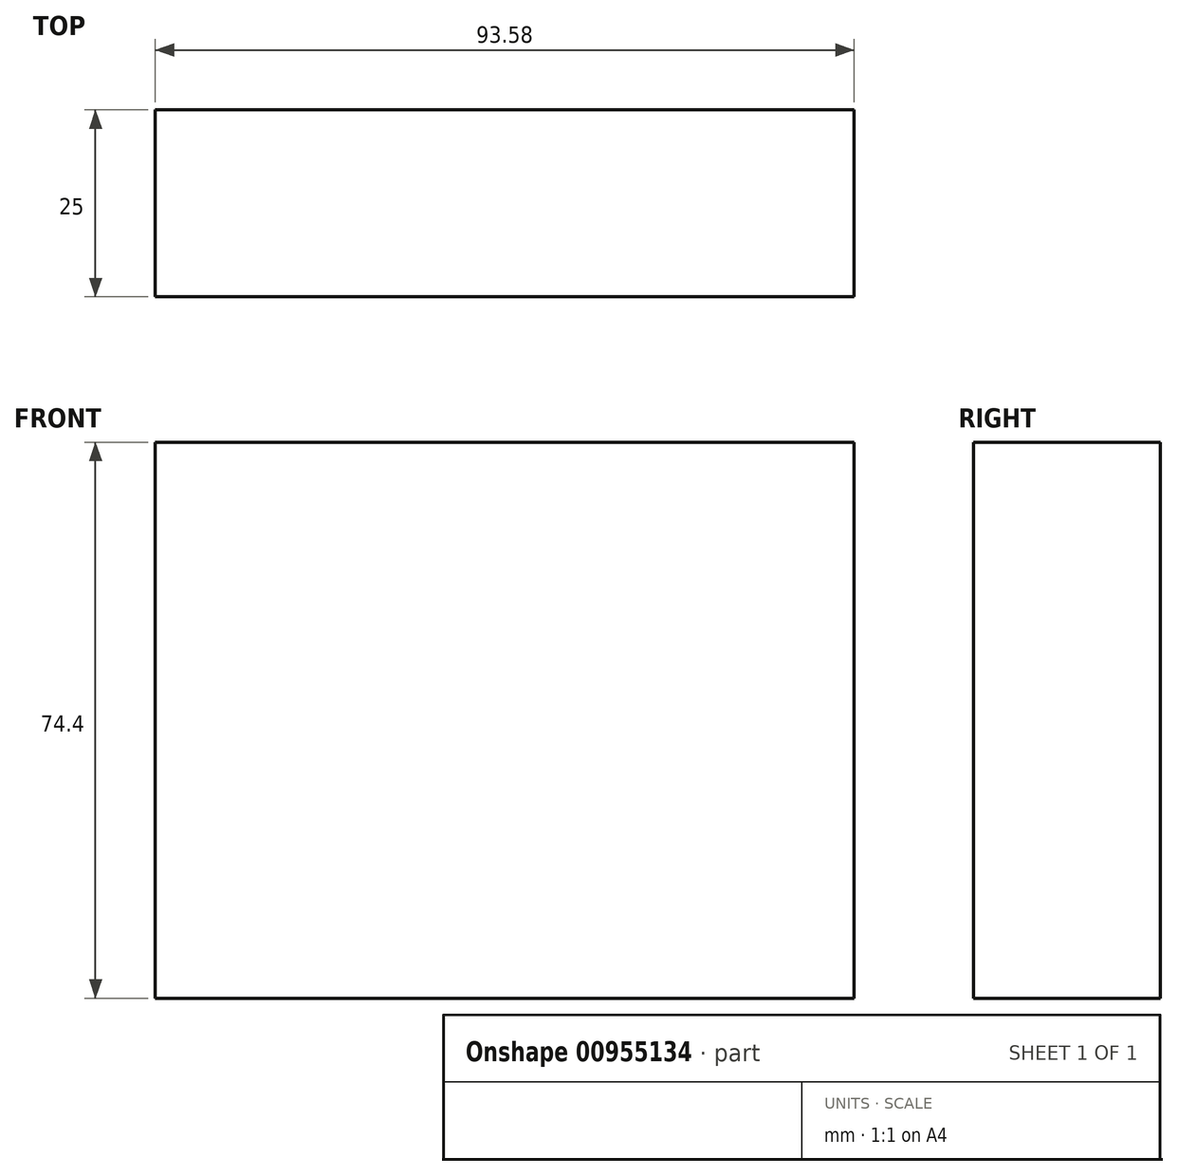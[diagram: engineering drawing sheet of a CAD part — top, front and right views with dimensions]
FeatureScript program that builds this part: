
annotation { "Feature Type Name" : "Feature", "Feature Type Description" : "" }
export const myFeature = defineFeature(function(context is Context, id is Id, definition is map)
    precondition{}
    {
        {
            var Q0;
            Q0=qCreatedBy(makeId("Front.planeOp"),FACE);
            var sketch = newSketch(context, id + "F0", { "sketchPlane" : qUnion([Q0])});
            skLineSegment(sketch, "E0.bottom", {"start": v(-99.12, 58.07) * mm, "end": v(-5.54, 58.07) * mm});
            skLineSegment(sketch, "E0.top", {"start": v(-99.12, -16.33) * mm, "end": v(-5.54, -16.33) * mm});
            skLineSegment(sketch, "E0.left", {"start": v(-99.12, 58.07) * mm, "end": v(-99.12, -16.33) * mm});
            skLineSegment(sketch, "E0.right", {"start": v(-5.54, 58.07) * mm, "end": v(-5.54, -16.33) * mm});
            skSolve(sketch);
        }
        {
            var Q0;
            Q0 = qSketchRegion(id + "F0", true);
            extrude(context, id + "F1", {"entities" : qUnion([Q0]), "depth" : 25 * mm, "offsetDistance" : 25 * mm});
        }
    });
